# Revit family: QF_ELECTROLUXPROFESSIONAL_1LSNJ9_IC64825LF_G
name_source: partatom
category: Attrezzature speciali
units: mm (PartAtom-declared; Revit-internal decimal feet)

## family parameters
Basato su piano di lavoro = No
Condiviso = No
Punto di calcolo locali = No
Quota connettore circolare = Usa diametro
Sempre verticale = Sì
Taglio con vuoti quando caricato = No
Tipo di parte = Normale

## types (6) — shared parameters
Cycle = 50 Hz
Depth Actual = 1110 mm
Gas KW = 52
Height Actual = 1270 mm  [stored 4.16667 ft]
Latent Heat Output = 0.0
Length Actual = 3205 mm
Modello = IC64825LF
Phase = 3
Produttore = Electrolux Professional
Sensible Heat Output = 0.0
URL = www.electroluxprofessional.com
Volts = 400 V
Watts = 1400 W
Weight = 875
zero-valued in all types: Prospetto di default, Steam Pounds per Hour

## per-type parameters (varying)
| type | Descrizione | Item Number |
| 9882030110 | IRONER CYLINDER IC64825LF LENGTH FOLDING 2540MM GAS CE 400/50/3 6MM SST CYL. FR VAC.FEED.TABLE | 1L0GL1 |
| 9882030171 | IRONER CYLINDER IC64825LF LENGTH FOLDING 2540MM PERFORMANCE GAS CE 400/50/3 DUBIXIUM ML VAC.FEED.TABLE DIAMMS | 1LSPEE |
| 9882030168 | IRONER CYLINDER IC64825LF LENGTH FOLDING 2540MM PERFORMANCE GAS CE 400/50/3 DUBIXIUM FR VAC.FEED.TABLE DIAMMS | 1LD05S |
| 9882030033 | IRONER CYLINDER IC64825LF LENGTH FOLDING 2540MM GAS CE 400/50/3 DUBIXIUM ML ANTISTATIC DIAMMS | 1LA09D |
| 9882030242 | IRONER CYLINDER IC64825LF LENGTH FOLDING 2540MM ACTIVE GAS CE 400/50/3 6MM SST CYL. FR FEED NOW | 1L0GWF |
| 9882030179 | IRONER CYLINDER IC64825LF LENGTH FOLDING 2540MM GAS CE 400/50/3 6MM SST CYL. ML FEED NOW FEED ALONE VAC.FEED.TABLE ANTIS | 1L0GRY |

note: [stored X ft] marks values corroborated as IEEE doubles in the binary element streams (Revit-internal decimal feet)

## geometry (parser evidence)
native form markers: Sweep x11
no freeform markers — native parametric forms only
